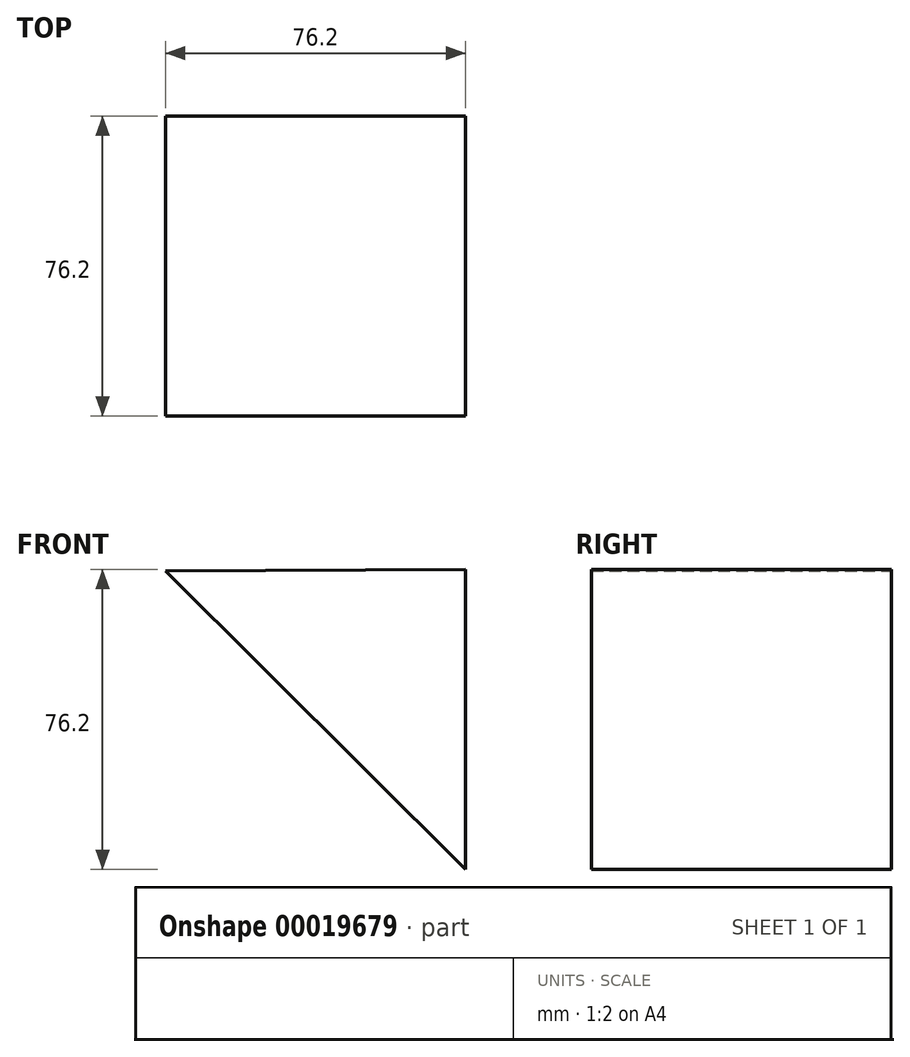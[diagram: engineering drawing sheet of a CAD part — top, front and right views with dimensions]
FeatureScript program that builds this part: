
annotation { "Feature Type Name" : "Feature", "Feature Type Description" : "" }
export const myFeature = defineFeature(function(context is Context, id is Id, definition is map)
    precondition{}
    {
        {
            var Q0;
            Q0=qCreatedBy(makeId("Front.planeOp"),FACE);
            var sketch = newSketch(context, id + "F0", { "sketchPlane" : qUnion([Q0])});
            skLineSegment(sketch, "E0", {"start": v(3.14, 0) * mm, "end": v(3.14, 75.85) * mm});
            skLineSegment(sketch, "E1", {"start": v(3.14, 0) * mm, "end": v(79.34, 0) * mm});
            skLineSegment(sketch, "E2", {"start": v(79.34, 0) * mm, "end": v(79.34, 76.2) * mm});
            skLineSegment(sketch, "E3", {"start": v(3.14, 75.85) * mm, "end": v(79.34, 76.2) * mm});
            skLineSegment(sketch, "E4", {"start": v(3.14, 75.85) * mm, "end": v(79.34, 0) * mm});
            skSolve(sketch);
        }
        {
            var Q0;
            Q0=makeQuery(id+"F0.imprint","IMPRINT",FACE,{"disambiguationData":[TD([[makeQuery(id+"F0.imprint","IMPRINT",EDGE,{"derivedFrom":sQuery(id+"F0.wireOp",EDGE,"E2")}),1.0]])]});
            extrude(context, id + "F1", {"entities" : qUnion([Q0]), "depth" : 76.2 * mm});
        }
    });
